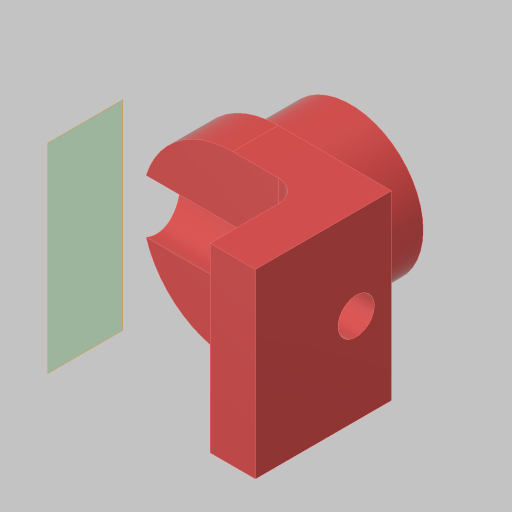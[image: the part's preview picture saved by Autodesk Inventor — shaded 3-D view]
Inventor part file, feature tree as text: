
AUTODESK INVENTOR PART (.ipt)
format: ipt  version: 2023.5 (Build 275446000, 446)  size: 177,664 bytes
history: native  units: in
note: dims shown in document units (in); Inventor stores cm internally (conversion verified against a paired STEP export)
features: sketch x6, extrude x4, projected_geometry x3, hole x2, fillet x1, plane x1
ambient origin geometry x8: Origin, YZ Plane, XZ Plane, XY Plane, X Axis, Y Axis, Z Axis, Center Point
bodies: Solid1 (feature_tree)
feature tree (17):
  extrude  "Extrusion1"  Depth=0.4in TaperAngle=0.0deg
  extrude  "Extrusion2"  Depth=0.25in TaperAngle=0.0deg
  hole  "Hole2"  [1 undecoded]
  extrude  "Extrusion3"  Depth=0.5in
  fillet  "Fillet1"  Radius=0.5in
  hole  "Hole3"  [1 undecoded]
  plane  "Work Plane1"
  extrude  "Extrusion4"  Depth=0.25in
  sketch  "Sketch1"  dims[d0=0.8in d1=0.4in d2=0.0in]
  sketch  "Sketch2"  dims[d3=0.1in d4=0.25in d5=0.0in]
  sketch  "Sketch4"  dims[d6=0.688in d14=0.625in]
  sketch  "Sketch5"  dims[d15=0.257in d16=0.75in d17=0.375in d18=0.25in d19=0.5635in d20=1.0in d21=0.8108in d22=0.25in d23=0.5in d24=0.0in]
  sketch  "Sketch6"  dims[d25=0.125in d26=0.5in]
  sketch  "Sketch7"  dims[d27=0.201in d28=0.38in d29=0.385in d30=0.25in d31=0.5635in d32=1.0in d33=0.8108in d34=0.25in d35=1.0in d36=0.555in d37=0.875in d38=0.315in d39=0.8in d40=0.0in]
  projected_geometry  "Project Cut Edges1"
  projected_geometry  "Project Cut Edges2"
  projected_geometry  "Project Cut Edges3"
note: 2 required parameter values undecoded (feature->parameter linkage not recoverable at this tier; creation-order binding heuristic only, values carry confidence <= 0.55)
